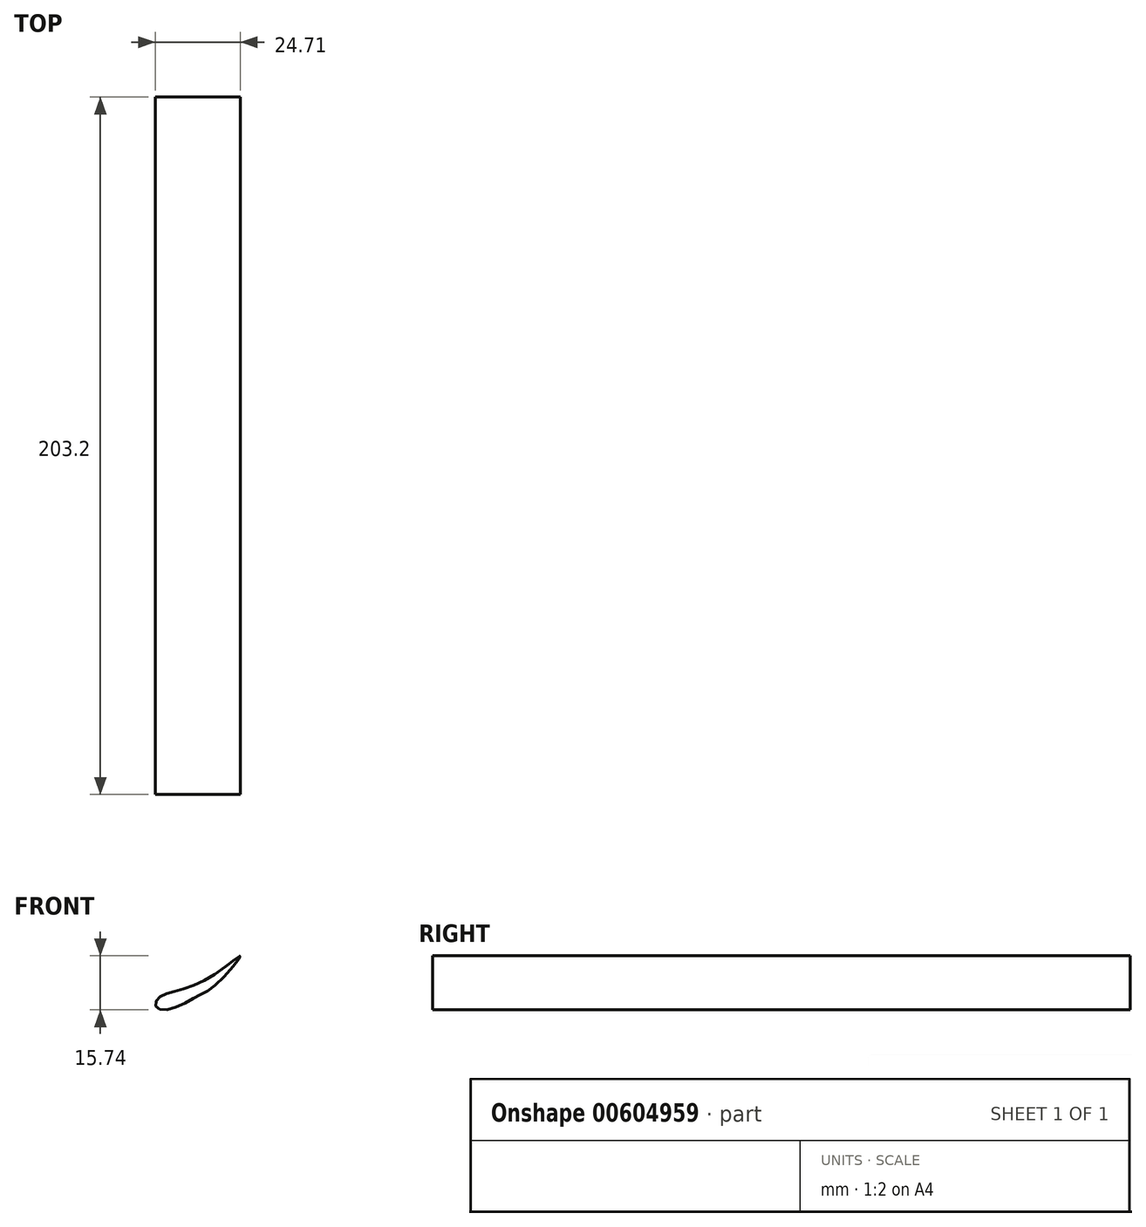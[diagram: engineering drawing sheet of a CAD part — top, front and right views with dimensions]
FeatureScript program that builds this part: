
annotation { "Feature Type Name" : "Feature", "Feature Type Description" : "" }
export const myFeature = defineFeature(function(context is Context, id is Id, definition is map)
    precondition{}
    {
        {
            var Q0;
            Q0=qCreatedBy(makeId("Front.planeOp"),FACE);
            var sketch = newSketch(context, id + "F0", { "sketchPlane" : qUnion([Q0])});
            skFitSpline(sketch, "E0", {"points": [v(-14.75, 12.7) * mm, v(-13.72, 15.26) * mm, v(-8.08, 17.3) * mm, v(3.2, 22.44) * mm, v(9.87, 27.31) * mm, v(2.95, 19.1) * mm, v(-3.2, 15.26) * mm, v(-11.41, 11.67) * mm, v(-14.75, 12.7) * mm]});
            skSolve(sketch);
        }
        {
            var Q0;
            Q0=makeQuery(id+"F0.imprint","IMPRINT",FACE,{"disambiguationData":[TD([[makeQuery(id+"F0.imprint","IMPRINT",EDGE,{"derivedFrom":sQuery(id+"F0.wireOp",EDGE,"E0")}),-1.0]])]});
            extrude(context, id + "F1", {"entities" : qUnion([Q0]), "depth" : 76.2 * mm, "offsetDistance" : 25.4 * mm});
        }
        {
            var Q0;
            Q0=makeQuery(id+"F1.opExtrude","CAP_FACE",FACE,{"disambiguationData":[OSD([sQuery(id+"F0.wireOp",EDGE,"E0")])],"isStart":false});
            extrude(context, id + "F2", {"entities" : qUnion([Q0]), "operationType" : NewBodyOperationType.ADD, "depth" : 25.4 * mm, "offsetDistance" : 25.4 * mm, "hasSecondDirection" : true, "secondDirectionOppositeDirection" : true, "secondDirectionDepth" : 152.4 * mm});
        }
        {
            var Q0;
            Q0=makeQuery(id+"F2.opExtrude","CAP_FACE",FACE,{"disambiguationData":[OSD([sQuery(id+"F0.wireOp",EDGE,"E0")])],"isStart":false});
            extrude(context, id + "F3", {"entities" : qUnion([Q0]), "operationType" : NewBodyOperationType.ADD, "depth" : 0 * mm, "offsetDistance" : 25.4 * mm, "hasSecondDirection" : true, "secondDirectionOppositeDirection" : true, "secondDirectionDepth" : 25.4 * mm});
        }
        {
            var Q0;
            Q0=makeQuery(id+"F2.opExtrude","CAP_FACE",FACE,{"disambiguationData":[OSD([sQuery(id+"F0.wireOp",EDGE,"E0")])],"isStart":false});
            extrude(context, id + "F4", {"entities" : qUnion([Q0]), "operationType" : NewBodyOperationType.ADD, "depth" : -25.4 * mm, "offsetDistance" : 25.4 * mm});
        }
        {
            var Q0;
            Q0=makeQuery(id+"F2.opExtrude","CAP_FACE",FACE,{"disambiguationData":[OSD([sQuery(id+"F0.wireOp",EDGE,"E0")])],"isStart":true});
            extrude(context, id + "F5", {"entities" : qUnion([Q0]), "operationType" : NewBodyOperationType.ADD, "depth" : 25.4 * mm, "offsetDistance" : 25.4 * mm});
        }
    });
